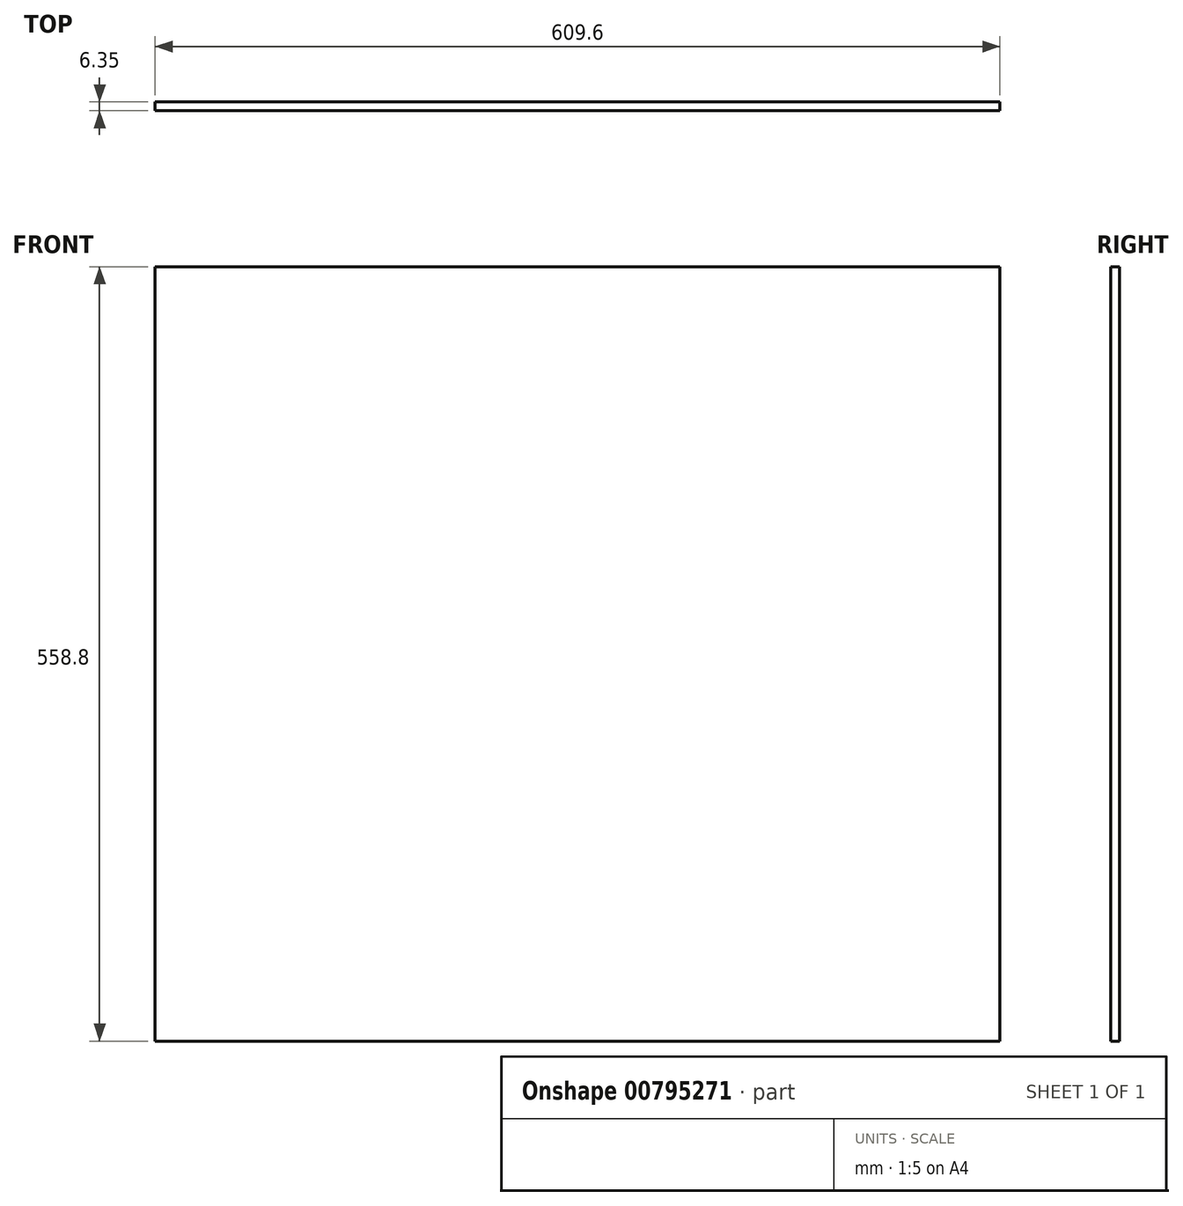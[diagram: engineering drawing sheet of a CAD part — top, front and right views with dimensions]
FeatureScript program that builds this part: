
annotation { "Feature Type Name" : "Feature", "Feature Type Description" : "" }
export const myFeature = defineFeature(function(context is Context, id is Id, definition is map)
    precondition{}
    {
        {
            var Q0;
            Q0=qCreatedBy(makeId("Front.planeOp"),FACE);
            var sketch = newSketch(context, id + "F0", { "sketchPlane" : qUnion([Q0])});
            skLineSegment(sketch, "E0.bottom", {"start": v(304.8, -279.4) * mm, "end": v(-304.8, -279.4) * mm});
            skLineSegment(sketch, "E0.top", {"start": v(304.8, 279.4) * mm, "end": v(-304.8, 279.4) * mm});
            skLineSegment(sketch, "E0.left", {"start": v(304.8, -279.4) * mm, "end": v(304.8, 279.4) * mm});
            skLineSegment(sketch, "E0.right", {"start": v(-304.8, -279.4) * mm, "end": v(-304.8, 279.4) * mm});
            skPoint(sketch, "E0.middle", {"position": v(0, 0) * mm});
            skSolve(sketch);
        }
        {
            var Q0;
            Q0=makeQuery(id+"F0.imprint","IMPRINT",FACE,{"disambiguationData":[TD([[makeQuery(id+"F0.imprint","IMPRINT",EDGE,{"derivedFrom":sQuery(id+"F0.wireOp",EDGE,"E0.bottom")}),-1.0]])]});
            extrude(context, id + "F1", {"entities" : qUnion([Q0]), "depth" : 6.35 * mm, "offsetDistance" : 25.4 * mm});
        }
    });
